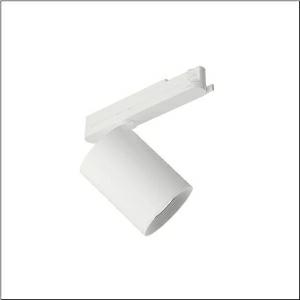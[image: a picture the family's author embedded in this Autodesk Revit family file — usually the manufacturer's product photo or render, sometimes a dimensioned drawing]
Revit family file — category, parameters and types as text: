
# Revit family: spot_11_51sd14ebd5a
name_source: partatom
category: Lighting Fixtures
units: mm (PartAtom-declared; Revit-internal decimal feet)

## family parameters
Cut with Voids When Loaded = No
Host = Face
Light Source = No
Part Type = Normal
Room Calculation Point = No
Round Connector Dimension = Use Diameter
Shared = No

## types (1)
- --- (1 x LED, 7420 lm, 51.1 W, 4000K)
    Apparent Load = 51 VA
    CIE Flux Codes = 95 98 100 100 100
    Color Rendering = 90
    Color Temperature = 4000K
    Default Elevation = 1800 mm
    Description = Spot 11, directional spotlight, light control with lens, of PMMA, LED rated luminous flux: 5.670lm, light colour: 940, control gear: ECG Multilumen, with 3-phase adapter, mains connection: 220..240V, AC, 50/60Hz, of aluminium, traffic white (RAL 9016), length: 253mm, diameter: 105mm, protection rating (complete): IP20, insulation class (complete): insulation class I (protective earthing), certification: CE, impact resistance: IK02, permissible ambient temperature for indoor applications: -20..+40°C, packaging unit: 1 piece
    Height = 175 mm
    Lamp = 1 x LED
    Lamp Light Flux = 7420 lm
    Lamp Power = 51.1 W
    Lamp count = 1
    Length = 105 mm
    Luminous efficacy = 145 lm/W
    Manufacturer = Siteco
    ModVariant = No
    Model = 51SD14EBD5A
    Mounting Place = Ceiling
    Mounting Type = Pendant
    Number of Poles = 1
    OnlyDefault = Yes
    Power Factor = 1
    Product Name = Spot 11
    Product group = directional spotlight
    ProductGroupID = 906
    Protection Class = Protection class I
    Protection Degree = IP 20
    RLX_Detail_Level = 1
    RLX_Emergency_Light_Flux = 0 lm
    RLX_Emergency_Type = 0
    RLX_Emergency_Type_DB = No
    RlxData = <blob elided: 17613 chars, md5=4efa573a>
    Socket = socket
    Standby Power = 0 W
    System Light Flux = 7420 lm
    System Power = 51 W
    Type Comments = factory setting: luminous flux: 100 % | (ON | ON | ON | ON) | 1050 mA
    Type Image = l_1006697.jpg
    URL = http://relux.com
    VarID = @adj_147386
    Voltage = 0 V
    Weight = 0.00 kg
    Width = 0 mm  [stored 0 ft]

note: [stored X ft] marks values corroborated as IEEE doubles in the binary element streams (Revit-internal decimal feet)

## geometry (parser evidence)
native form markers: Blend x4, Sweep x11
no freeform markers — native parametric forms only
